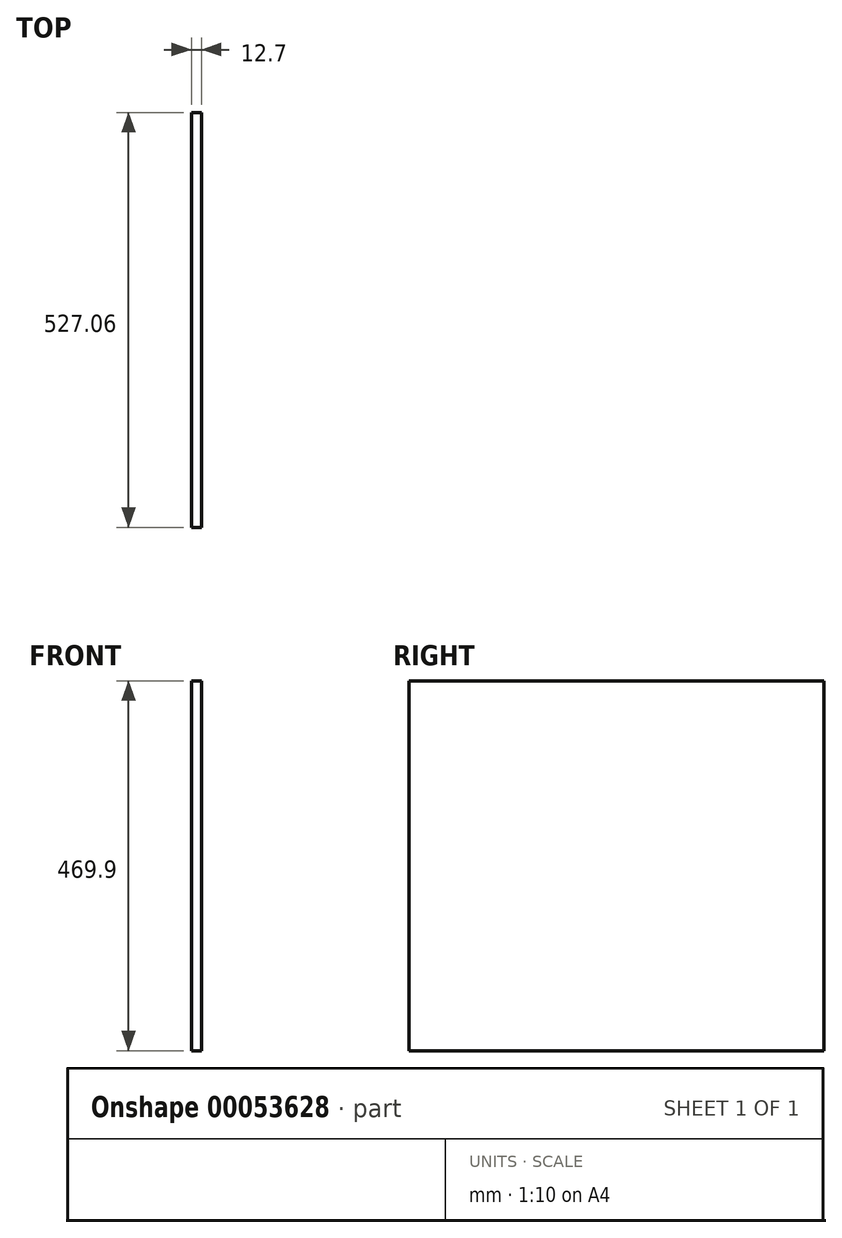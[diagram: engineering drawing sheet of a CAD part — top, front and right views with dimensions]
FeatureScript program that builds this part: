
annotation { "Feature Type Name" : "Feature", "Feature Type Description" : "" }
export const myFeature = defineFeature(function(context is Context, id is Id, definition is map)
    precondition{}
    {
        {
            var Q0;
            Q0=qCreatedBy(makeId("Right.planeOp"),FACE);
            var sketch = newSketch(context, id + "F0", { "sketchPlane" : qUnion([Q0])});
            skLineSegment(sketch, "E0.bottom", {"start": v(-263.53, 234.95) * mm, "end": v(263.53, 234.95) * mm});
            skLineSegment(sketch, "E0.top", {"start": v(-263.53, -234.95) * mm, "end": v(263.53, -234.95) * mm});
            skLineSegment(sketch, "E0.left", {"start": v(-263.53, 234.95) * mm, "end": v(-263.53, -234.95) * mm});
            skLineSegment(sketch, "E0.right", {"start": v(263.53, 234.95) * mm, "end": v(263.53, -234.95) * mm});
            skSolve(sketch);
        }
        {
            var Q0;
            Q0=makeQuery(id+"F0.imprint","IMPRINT",FACE,{"disambiguationData":[TD([[makeQuery(id+"F0.imprint","IMPRINT",EDGE,{"derivedFrom":sQuery(id+"F0.wireOp",EDGE,"E0.bottom")}),-1.0]])]});
            extrude(context, id + "F1", {"entities" : qUnion([Q0]), "depth" : 12.7 * mm});
        }
    });
